# Revit family: Izveshchatel okhrannyy tochechnyy magnitokontaktnyy IO 102-555
name_source: partatom
category: Датчики
units: mm (PartAtom-declared; Revit-internal decimal feet)

## family parameters
Всегда вертикально = Да
Заголовок OmniClass = Communication and Data Processing Equipment
На основе рабочей плоскости = Нет
Номер OmniClass = 23.85.50.17
Общий = Нет
При загрузке вырезать с полостями = Нет
Размер круглого соединителя = Использовать диаметр
Сохранять ориентацию аннотаций = Нет
Тип детали = Нормальный
Точка принадлежности помещению = Нет

## types (1)
- Извещатель охранный точечный магнитоконтактный ИО102-555
    ADSK_Единица измерения = шт.
    ADSK_Завод-изготовитель = ООО НПП «МАГНИТО-КОНТАКТ»
    ADSK_Масса = 0
    ADSK_Материал = ABS пластик
    ADSK_Наименование = Извещатель охранный точечный магнитоконтактный ИО102-555
    ADSK_Наименование краткое = ИО102-555
    ADSK_Обозначение = ПАШК.425119.111
    ADSK_Примечание = Извещатели предназначены для открытой установки на поверхности охраняемой конструкции.
    ADSK_Размер_Высота = 10 мм
    ADSK_Размер_Длина = 20 мм
    ADSK_Размер_Ширина = 15 мм
    URL = https://m-kontakt.ru
    Изготовитель = ООО НПП «МАГНИТО-КОНТАКТ»
    Кабельный вывод = Кабельный вывод
    Максимальная мощность = 10 Вт.
    Напряжение = от 0,02 до 72 В.
    Описание = Извещатели охранные точечные магнитоконтактные ИО102-555 (далее извещатели) предназначены для блокировки дверных и оконных проемов, организации устройств типа «ловушка», а также блокировки других конструктивных элементов зданий и сооружений на открывание или смещение с выдачей извещения о тревоге на пульт централизованного наблюдения, прибор приёмно-контрольный или концентратор размыканием шлейфа сигнализации контактами встроенного геркона.
    Отметка по умолчанию = 0 мм
    Провод = Да
    Срок службы = не менее 8 лет.
    Степень защиты оболочки = IP66
